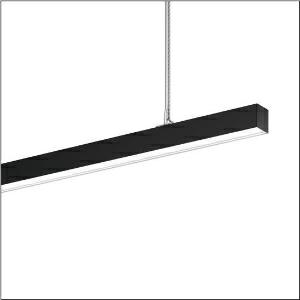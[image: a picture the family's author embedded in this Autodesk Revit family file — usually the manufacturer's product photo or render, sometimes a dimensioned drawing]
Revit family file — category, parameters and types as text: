
# Revit family: silica_r__21_51mx33da47bb_630a
name_source: partatom
category: Lighting Fixtures
units: mm (PartAtom-declared; Revit-internal decimal feet)

## family parameters
Cut with Voids When Loaded = No
Host = Face
Light Source = No
Part Type = Normal
Room Calculation Point = No
Round Connector Dimension = Use Diameter
Shared = No

## types (1)
- --- (1 x LED, 5910 lm, 38.4 W, 4000K)
    Apparent Load = 38 VA
    CIE Flux Codes = 78 96 99 55 100
    Color Rendering = 80
    Color Temperature = 4000K
    Default Elevation = 1800 mm
    Description = Silica® 21, office luminaire, primary optical cover: prismatic diffuser, of PMMA, CAT 2 (L<= 3000cd/m²), light emission: direct/indirect distribution, primary light characteristic: symmetric, installation type: suspended mounting, LED, rated luminous flux: 5.910lm, luminous efficacy: 154lm/W, light colour: 840, colour temperature: 4000K, with terminal, 3+2-pole, max. 2.5mm², mains connection: 220..240V, AC, 50/60Hz, rated input power: 38.4W, luminaire housing, of aluminium, jet black (RAL 9005), length: 1.204mm, width: 53mm, height: 53mm, protection rating (complete): IP20, insulation class (complete): insulation class I (protective earthing), certification: CE, permissible operating ambient temperature: 0..+35°C, standard: EN 50419, packaging unit: 1 piece
    Height = 53 mm
    Lamp = 1 x LED
    Lamp Light Flux = 5910 lm
    Lamp Power = 38.4 W
    Lamp count = 1
    Length = 1204 mm
    Luminous efficacy = 154 lm/W
    Manufacturer = Siteco
    ModVariant = No
    Model = 51MX33DA47BB
    Mounting Place = Ceiling
    Mounting Type = Pendant
    Number of Poles = 1
    OnlyDefault = Yes
    Power Factor = 1
    Product Name = Silica® 21
    Product group = office luminaire | ceiling pendant
    ProductGroupID = 902
    Protection Class = Protection class I
    Protection Degree = IP 20
    RLX_Detail_Level = 1
    RLX_Emergency_Light_Flux = 0 lm
    RLX_Emergency_Type = 0
    RLX_Emergency_Type_DB = No
    RlxData = <blob elided: 25889 chars, md5=5e2ebf0d>
    Socket = socket
    Standby Power = 0 W
    System Light Flux = 5910 lm
    System Power = 38 W
    Type Comments = factory setting: luminous flux: 100 % | dim-lin: 254 | 323 mA
    Type Image = l_1313646.jpg
    URL = http://relux.com
    VarID = @adj_067271
    Voltage = 0 V
    Weight = 0.00 kg
    Width = 53 mm

## geometry (parser evidence)
native form markers: Blend x4, Sweep x13
no freeform markers — native parametric forms only
